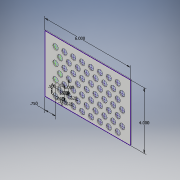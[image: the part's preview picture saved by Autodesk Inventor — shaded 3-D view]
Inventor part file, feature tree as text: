
AUTODESK INVENTOR PART (.ipt)
format: ipt  version: 2017 (Build 210142000, 142)  size: 219,136 bytes
history: native  units: in
note: dims shown in document units (in); Inventor stores cm internally (conversion verified against a paired STEP export)
features: sketch x1, extrude x1, hole x1
ambient origin geometry x8: Origin, YZ Plane, XZ Plane, XY Plane, X Axis, Y Axis, Z Axis, Center Point
bodies: Solid1 (feature_tree)
feature tree (3):
  sketch  "Sketch1"  dims[d0=6.0in d1=4.0in d2=0.375in d3=0.75in d4=3.1496in d6=0.625in d7=0.3937in d9=1.0in d11=0.5in d12=0.3125in d13=3.1496in d15=0.625in d16=0.3937in d18=1.0in d20=2.7559in d22=0.625in d23=1.5748in d25=1.0in d28=2.7559in d30=0.625in d31=1.1811in d33=1.0in d36=0.06in d37=0.0in d38=0.375in d39=0.75in d40=0.375in d41=0.25in d42=0.5635in d43=1.0in d44=0.8108in]
  extrude  "Extrusion1"  Depth=4.0in
  hole  "Hole1"  [1 undecoded]
note: 1 required parameter value undecoded (feature->parameter linkage not recoverable at this tier; creation-order binding heuristic only, values carry confidence <= 0.55)
